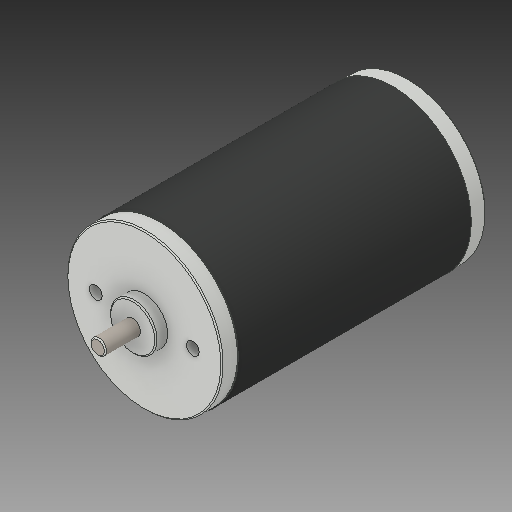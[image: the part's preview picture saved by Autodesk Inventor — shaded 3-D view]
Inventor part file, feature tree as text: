
AUTODESK INVENTOR PART (.ipt)
format: ipt  version: 2017 (Build 210142000, 142)  size: 138,752 bytes
history: native  units: in
note: dims shown in document units (in); Inventor stores cm internally (conversion verified against a paired STEP export)
features: chamfer x1
ambient origin geometry x8: Origin, YZ Plane, XZ Plane, XY Plane, X Axis, Y Axis, Z Axis, Center Point
bodies: Solid1 (feature_tree)
feature tree (1):
  chamfer  "Chamfer1"  [1 undecoded]
note: 1 required parameter value undecoded (feature->parameter linkage not recoverable at this tier; creation-order binding heuristic only, values carry confidence <= 0.55)
